# Revit family: Grohe_ShowerSystemWithThermostat_266702431
name_source: partatom
category: Plumbing Fixtures
units: mm (PartAtom-declared; Revit-internal decimal feet)

## family parameters
Cut with Voids When Loaded = No
Host = Face
OmniClass Number = 23.45.05.00
OmniClass Title = Sanitary Equipment
Part Type = Normal
Room Calculation Point = No
Round Connector Dimension = Use Diameter
Shared = No

## types (1)
- Shower System With Thermostat (266702431)
    Assembly Code = D2013
    AssetType = Fixed
    BIMObjectName = Grohe_ShowerSystemWithThermostat_266702431
    CO2NeutralProduction = GROHE is one of the first leading manufacturer within the sanitary industry having a CO2-neutral production.
    ClassificationName = Uniclass2015
    ClassificationValue = Pr_40_20_87_55
    Color = Grohe_Chrome
    Cost = 0 $
    Default Elevation = 0 mm  [stored 0 ft]
    Description = Shower System With Thermostat
    DimensionsDocumentLink = https://cdn.cloud.grohe.com
    DocumentationCertificates = https://www.bimstore.co
    DocumentationInstallationGuide = https://www.bimstore.co
    DocumentationLiterature = https://www.bimstore.co
    DocumentationMaintenance = https://www.bimstore.co
    DocumentationTechnical = https://www.bimstore.co
    DurationUnit = Years
    EF000008 = 0 mm  [stored 0 ft]
    EF000040 = 0 mm  [stored 0 ft]
    EF000049 = 0 mm  [stored 0 ft]
    EF000551 = 0 mm  [stored 0 ft]
    EF000634 = 0.0 Pa
    EF001707 = 0 °C
    EF002169 = Aluminium/plastic
    EF002286 = Insert (push coupling)
    EF002671 = Black
    EF003454 = false
    EF003829 = false
    EF005084 = Wall
    EF006009 = true
    EF006013 = false
    EF006974 = Thermostatic
    EF020103 = false
    EF020785 = M26 x 1.5
    EF021457 = false
    EF021607 = true
    EF021720 = true
    EF021760 = true
    EF022168 = TRUE
    EF022284 = false
    EF023051 = Mechanical
    EF023061 = 0.0 Pa
    EF023686 = Other
    EF023957 = TRUE
    EF024792 = false
    EF024885 = true
    EF024921 = true
    EF025090 = false
    EF025091 = false
    EF025092 = 0
    EF025093 = not applicable
    EF025094 = 0
    EF025095 = not applicable
    EF025096 = true
    EFSE0002 = true
    Ecojoy = No
    ExpectedLife = 0
    FaucetMaterial = Grohe-Chrome
    Finish = Chrome
    FullRecyclabilityOfPlastic = All plastic components are fully recycable
    GROHESocialCommittment = green.grohe.com/social_engagement
    GROHESustainability = green.grohe.com
    IfcExportAs = IfcPipeFitting
    IfcExportType = IfcPipeFittingType
    Keynote = N16
    Manufacturer = Grohe
    ManufacturerName = Grohe
    Model = Shower System With Thermostat
    ModelNumber = 266702431
    ModelReference = Shower System With Thermostat
    NBSDescription = Shower fittings package
    NBSObjectName = Grohe - Shower fittings package
    NBSReference = 45-35-70/302
    NominalDepth = 0 mm  [stored 0 ft]
    NominalHeight = 0 mm  [stored 0 ft]
    NominalLength = 0 mm  [stored 0 ft]
    PrimaryMaterial = Grohe_Chrome
    ProductDescription = consisting of:

horizontal swivable 390 mm shower arm

exposed thermostat with Aquadimmer function

allows change between:

head shower Tempesta 250 (26 666)

spray pattern: Rain

head shower with white rear cover

with ball joint, rotation angle ± 10°

hand shower Tempesta 110 (27 597)

2 spray patterns: Rain, Jet

adjustable in height with gliding element

Rotaflex TwistStop shower hose 1750 mm 1/2" x 1/2" (28 410)

maximum flow rate (at 3 bar): 8.5 l/min

GROHE TurboStat compact cartridge with wax thermoelement

GROHE SafeStop safety button at 38°C

GROHE SafeStop Plus optional temperature limiter at 43°C included

GROHE SmartSwitch - easily rotate the dial to enjoy your preferred spray option

GROHE DreamSpray perfect spray pattern

GROHE Long-Life finish

SpeedClean anti-limescale system

Inner WaterGuide for a longer life

TwistStop to prevent hose from twisting

suitable for instantaneous heaters from 18 kW/h

minimum flow rate 7 l/min

optional upgrade: GROHE EasyReach tray (26 362), sold separately

professional exclusive
    ProductNumber = 266702431
    ProductShortText = Shower system with thermostat for wall mounting
    ProductType = Shower System
    ProductionYear = 2023
    SustainabilityAward = green.grohe.com/awards
    SustainabilityReport = green.grohe.com/reporting
    TPIDocumentLink = https://cdn.cloud.grohe.com
    Type Comments = Shower System With Thermostat
    TypeName = Shower System With Thermostat
    URL = https://www.grohe.co.uk
    WarrantyDurationLabor = 0
    WarrantyDurationParts = 0
    WarrantyDurationUnit = Years
    _BSBibleVersion = 17
    _BimSpecGuid = 0
    _CurrentRevision = 1
    _DistributedBy = https://www.bimstore.co
    _ObjectUserGuide = https://www.bimstore.co

note: [stored X ft] marks values corroborated as IEEE doubles in the binary element streams (Revit-internal decimal feet)

## geometry (parser evidence)
native form markers: Sweep x3
no freeform markers — native parametric forms only
